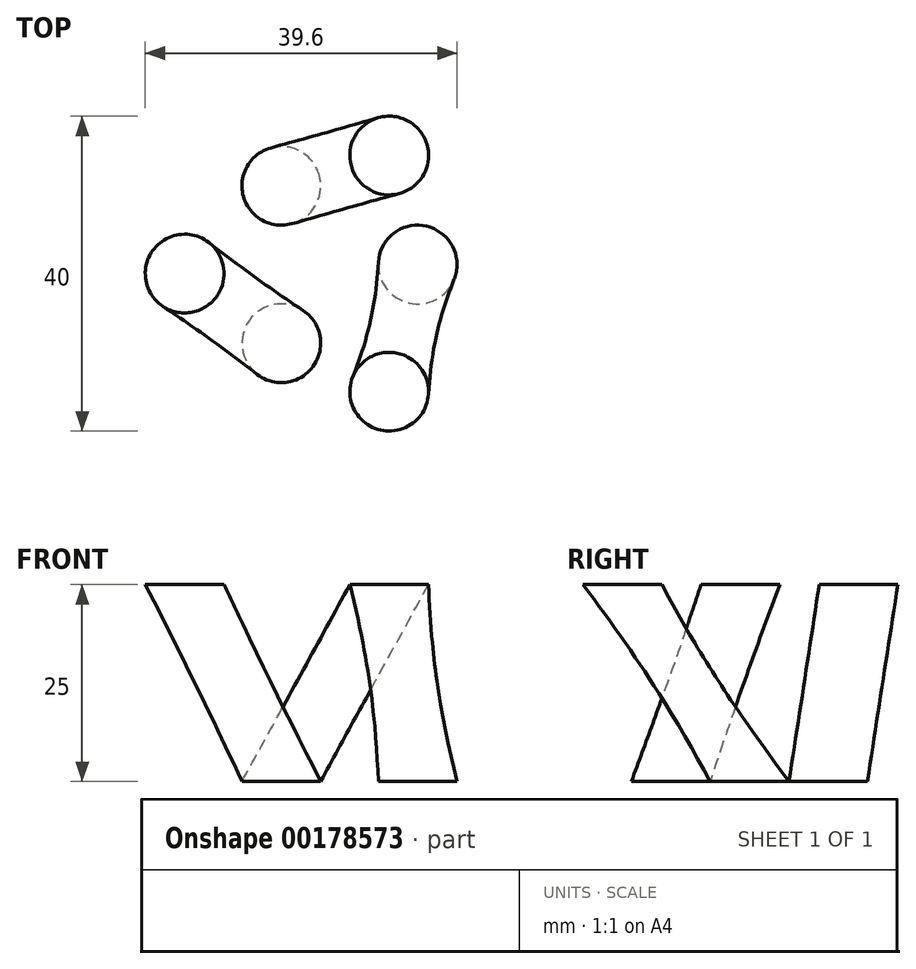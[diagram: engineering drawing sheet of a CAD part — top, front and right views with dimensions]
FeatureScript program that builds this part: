
annotation { "Feature Type Name" : "Feature", "Feature Type Description" : "" }
export const myFeature = defineFeature(function(context is Context, id is Id, definition is map)
    precondition{}
    {
        {
            var Q0;
            Q0=qCreatedBy(makeId("Top.planeOp"),FACE);
            var sketch = newSketch(context, id + "F0", { "sketchPlane" : qUnion([Q0])});
            skCircle(sketch, "E0", {"center": v(0, 0) * mm, "radius": 5 * mm});
            skCircle(sketch, "E1", {"center": v(0, -20) * mm, "radius": 5 * mm});
            skCircle(sketch, "E2", {"center": v(17.32, -10) * mm, "radius": 5 * mm});
            skSolve(sketch);
        }
        {
            var Q0;
            Q0=qCreatedBy(makeId("Top.planeOp"),FACE);
            cPlane(context, id + "F1", {"entities" : qUnion([Q0]), "cplaneType" : CPlaneType.OFFSET, "offset" : 25 * mm, "width" : 150 * mm, "height" : 150 * mm});
        }
        {
            var Q0;
            Q0=qCreatedBy(id+"F1.planeOp",FACE);
            var sketch = newSketch(context, id + "F2", { "sketchPlane" : qUnion([Q0])});
            skCircle(sketch, "E3", {"center": v(-12.28, -11.15) * mm, "radius": 5 * mm});
            skCircle(sketch, "E4", {"center": v(13.7, -26.15) * mm, "radius": 5 * mm});
            skCircle(sketch, "E5", {"center": v(13.7, 3.85) * mm, "radius": 5 * mm});
            skSolve(sketch);
        }
        {
            var Q0;
            Q0=makeQuery(id+"F0.imprint","IMPRINT",FACE,{"disambiguationData":[TD([[makeQuery(id+"F0.imprint","IMPRINT",EDGE,{"derivedFrom":sQuery(id+"F0.wireOp",EDGE,"E1")}),1.0]])]});
            var Q1;
            Q1=makeQuery(id+"F2.imprint","IMPRINT",FACE,{"disambiguationData":[TD([[makeQuery(id+"F2.imprint","IMPRINT",EDGE,{"derivedFrom":sQuery(id+"F2.wireOp",EDGE,"E3")}),1.0]])]});
            loft(context, id + "F3", {"sheetProfilesArray" : [{ "sheetProfileEntities" : qUnion([Q0]) }, { "sheetProfileEntities" : qUnion([Q1]) }]});
        }
        {
            var Q0;
            Q0=makeQuery(id+"F2.imprint","IMPRINT",FACE,{"disambiguationData":[TD([[makeQuery(id+"F2.imprint","IMPRINT",EDGE,{"derivedFrom":sQuery(id+"F2.wireOp",EDGE,"E5")}),1.0]])]});
            var Q1;
            Q1=makeQuery(id+"F0.imprint","IMPRINT",FACE,{"disambiguationData":[TD([[makeQuery(id+"F0.imprint","IMPRINT",EDGE,{"derivedFrom":sQuery(id+"F0.wireOp",EDGE,"E0")}),1.0]])]});
            loft(context, id + "F4", {"sheetProfilesArray" : [{ "sheetProfileEntities" : qUnion([Q0]) }, { "sheetProfileEntities" : qUnion([Q1]) }]});
        }
        {
            var Q0;
            Q0=makeQuery(id+"F0.imprint","IMPRINT",FACE,{"disambiguationData":[TD([[makeQuery(id+"F0.imprint","IMPRINT",EDGE,{"derivedFrom":sQuery(id+"F0.wireOp",EDGE,"E2")}),1.0]])]});
            var Q1;
            Q1=makeQuery(id+"F2.imprint","IMPRINT",FACE,{"disambiguationData":[TD([[makeQuery(id+"F2.imprint","IMPRINT",EDGE,{"derivedFrom":sQuery(id+"F2.wireOp",EDGE,"E4")}),1.0]])]});
            loft(context, id + "F5", {"sheetProfilesArray" : [{ "sheetProfileEntities" : qUnion([Q0]) }, { "sheetProfileEntities" : qUnion([Q1]) }]});
        }
    });
